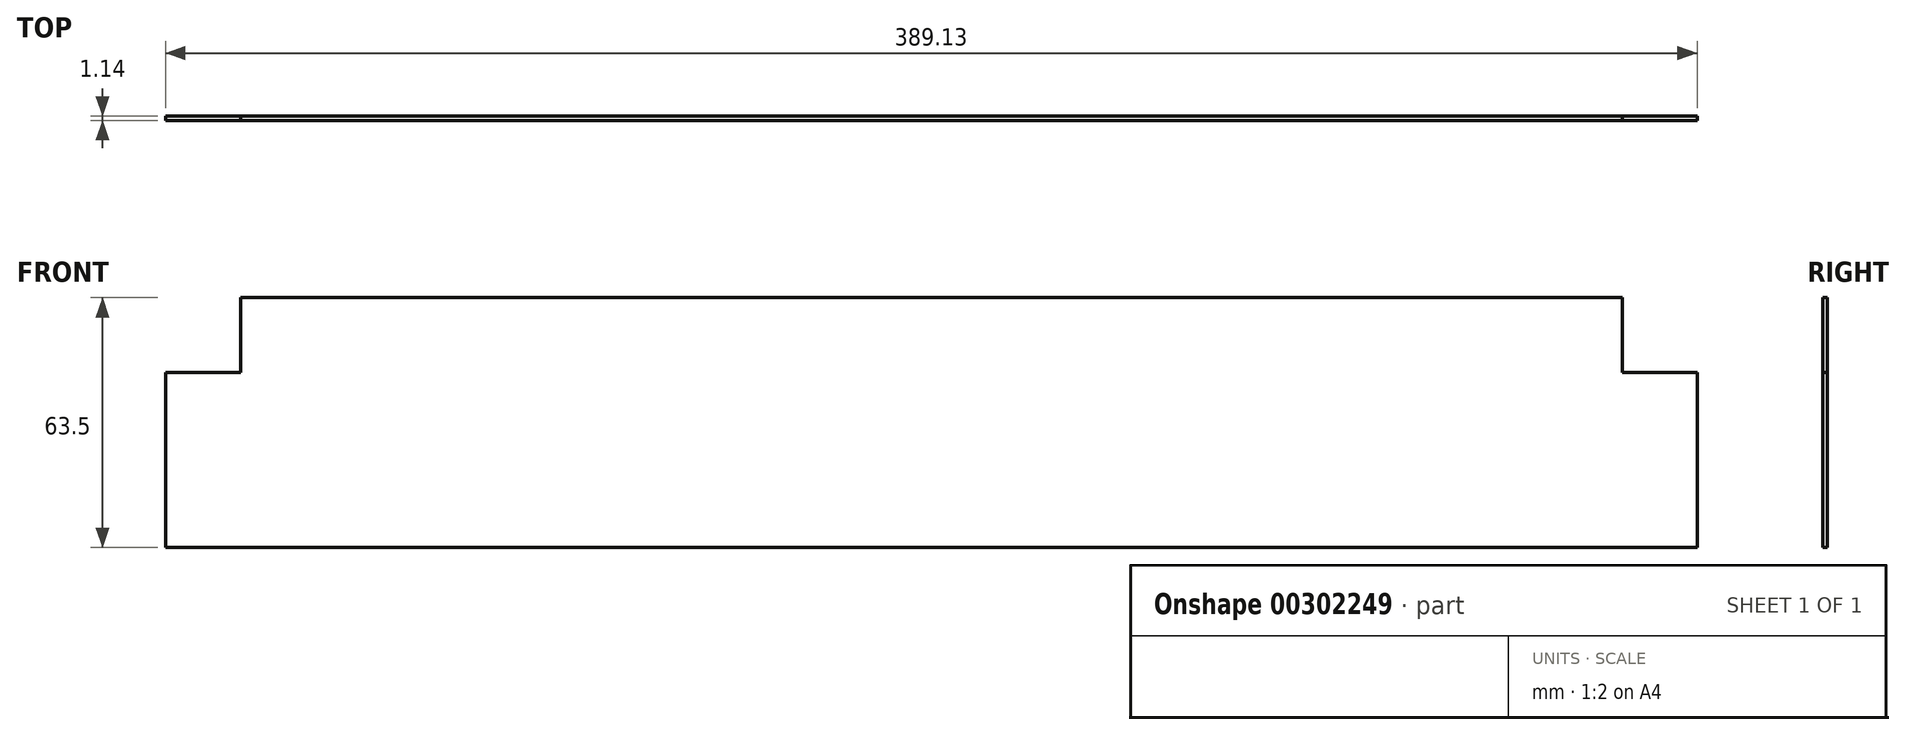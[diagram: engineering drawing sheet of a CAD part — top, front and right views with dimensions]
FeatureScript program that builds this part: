
annotation { "Feature Type Name" : "Feature", "Feature Type Description" : "" }
export const myFeature = defineFeature(function(context is Context, id is Id, definition is map)
    precondition{}
    {
        {
            var Q0;
            Q0=qCreatedBy(makeId("Front.planeOp"),FACE);
            var sketch = newSketch(context, id + "F0", { "sketchPlane" : qUnion([Q0])});
            skLineSegment(sketch, "E0.bottom", {"start": v(0, 0) * mm, "end": v(389.13, 0) * mm});
            skLineSegment(sketch, "E0.top", {"start": v(0, 63.5) * mm, "end": v(389.13, 63.5) * mm});
            skLineSegment(sketch, "E0.left", {"start": v(0, 0) * mm, "end": v(0, 63.5) * mm});
            skLineSegment(sketch, "E0.right", {"start": v(389.13, 0) * mm, "end": v(389.13, 63.5) * mm});
            skLineSegment(sketch, "E1.bottom", {"start": v(0, 63.5) * mm, "end": v(19.05, 63.5) * mm});
            skLineSegment(sketch, "E1.top", {"start": v(0, 44.45) * mm, "end": v(19.05, 44.45) * mm});
            skLineSegment(sketch, "E1.left", {"start": v(0, 63.5) * mm, "end": v(0, 44.45) * mm});
            skLineSegment(sketch, "E1.right", {"start": v(19.05, 63.5) * mm, "end": v(19.05, 44.45) * mm});
            skLineSegment(sketch, "E2.bottom", {"start": v(389.13, 63.5) * mm, "end": v(370.08, 63.5) * mm});
            skLineSegment(sketch, "E2.top", {"start": v(389.13, 44.45) * mm, "end": v(370.08, 44.45) * mm});
            skLineSegment(sketch, "E2.left", {"start": v(389.13, 63.5) * mm, "end": v(389.13, 44.45) * mm});
            skLineSegment(sketch, "E2.right", {"start": v(370.08, 63.5) * mm, "end": v(370.08, 44.45) * mm});
            skSolve(sketch);
        }
        {
            var Q0;
            Q0=makeQuery(id+"F0.imprint","IMPRINT",FACE,{"disambiguationData":[TD([[makeQuery(id+"F0.imprint","IMPRINT",EDGE,{"derivedFrom":sQuery(id+"F0.wireOp",EDGE,"E0.bottom")}),1.0]])]});
            extrude(context, id + "F1", {"entities" : qUnion([Q0]), "depth" : 1.14 * mm});
        }
    });
